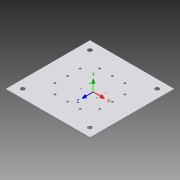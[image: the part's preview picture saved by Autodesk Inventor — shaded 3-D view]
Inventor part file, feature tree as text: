
AUTODESK INVENTOR PART (.ipt)
format: ipt  version: 2015 (Build 190159000, 159)  size: 241,664 bytes
history: native  units: in
note: dims shown in document units (in); Inventor stores cm internally (conversion verified against a paired STEP export)
features: other x10, sketch x5, hole x2, sheet_metal_op x1
ambient origin geometry x8: Origin, YZ Plane, XZ Plane, XY Plane, X Axis, Y Axis, Z Axis, Center Point
bodies: Solid1 (feature_tree)
feature tree (18):
  sheet_metal_op  "Face1"
  other  "UCS1"
  hole  "Hole1"  [1 undecoded]
  hole  "Hole2"  [1 undecoded]
  sketch  "Sketch9"  dims[d39=0.125in d40=0.75in d41=0.75in d42=5.313in d43=6.063in d44=11.376in d45=6.063in d46=0.25in d47=0.0in d48=4.2872in d49=5.9746in d50=6.063in d51=0.25in d52=8.3244in d53=4.2872in d54=0.125in d55=8.4494in d56=0.0625in d57=10.0in d58=10.0in d59=0.125in d60=8.0in d61=0.5in d62=0.5in d63=0.5in d64=0.5in d65=0.125in d66=0.0in d70=-2.5491in d71=0.0in d72=3.032in d73=0.0in d74=0.0in d75=0.0in d76=0.14in d77=0.75in d78=0.375in d79=0.25in d80=0.5635in d81=0.125in d82=0.8108in d83=0.144in d84=0.75in d85=0.279in d86=0.25in d87=0.5635in d88=0.125in d89=0.8108in d90=3.6662in d91=4.4695in]
  sketch  "Sketch1"  dims[d1=0.7874in d3=0.7874in d5=0.7874in d7=0.7874in d9=0.7874in d11=0.7874in d13=0.7874in d15=0.7874in d16=0.75in d17=0.75in d18=0.75in d19=0.75in d20=0.25in d21=0.25in d22=0.25in d23=0.25in d24=2.5681in d25=0.375in d26=1.5in d27=1.5in d28=1.5in d29=1.5in d30=1.5in d31=1.5in d32=1.5in d33=1.5in d34=90.0deg]
  other  "Plate1"
  sketch  "Sketch2"  dims[d35=45.0deg d36=90.0deg]
  sketch  "Sketch7"  dims[d37=90.0deg]
  sketch  "Sketch8"  dims[d38=90.0deg]
  other  "Cut1"
  other  "UCS1: YZ Plane"
  other  "UCS1: XZ Plane"
  other  "UCS1: XY Plane"
  other  "UCS1: X Axis"
  other  "UCS1: Y Axis"
  other  "UCS1: Z Axis"
  other  "UCS1: Center Point"
note: 2 required parameter values undecoded (feature->parameter linkage not recoverable at this tier; creation-order binding heuristic only, values carry confidence <= 0.55)
